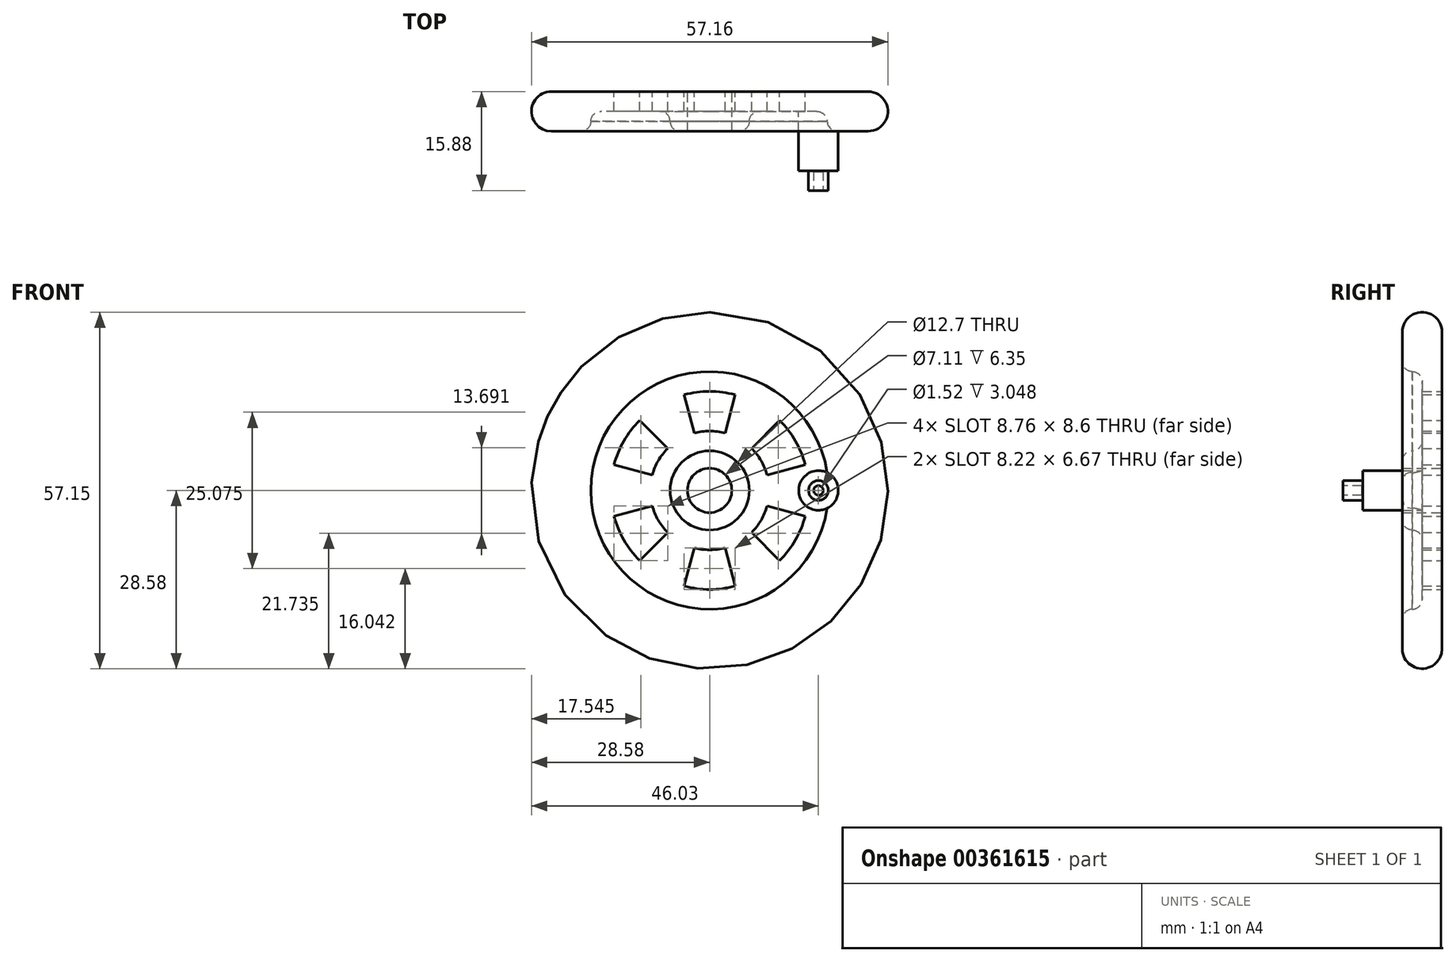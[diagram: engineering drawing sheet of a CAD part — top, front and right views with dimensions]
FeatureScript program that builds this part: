
annotation { "Feature Type Name" : "Feature", "Feature Type Description" : "" }
export const myFeature = defineFeature(function(context is Context, id is Id, definition is map)
    precondition{}
    {
        {
            var Q0;
            Q0=qCreatedBy(makeId("Top.planeOp"),FACE);
            var sketch = newSketch(context, id + "F0", { "sketchPlane" : qUnion([Q0])});
            skLineSegment(sketch, "E0", {"start": v(-3.56, 7.04) * mm, "end": v(-3.56, 0.69) * mm});
            skLineSegment(sketch, "E1", {"start": v(-3.56, 0.69) * mm, "end": v(-4.75, 0.69) * mm});
            skLineSegment(sketch, "E2", {"start": v(-6.35, 2.26) * mm, "end": v(-6.35, 2.29) * mm});
            skLineSegment(sketch, "E3", {"start": v(-7.95, 3.86) * mm, "end": v(-17.45, 3.86) * mm});
            skLineSegment(sketch, "E4", {"start": v(-19.05, 2.29) * mm, "end": v(-19.05, 2.26) * mm});
            skLineSegment(sketch, "E5", {"start": v(-20.65, 0.69) * mm, "end": v(-25.4, 0.69) * mm});
            skLineSegment(sketch, "E6", {"start": v(-25.4, 7.04) * mm, "end": v(-3.56, 7.04) * mm});
            skLineSegment(sketch, "E7", {"start": v(0, 5.87) * mm, "end": v(0, -4.8) * mm, "construction": true});
            skArc(sketch, "E8", {"start": v(-25.4, 7.04) * mm, "mid": v(-28.58, 3.86) * mm, "end": v(-25.4, 0.69) * mm});
            skPoint(sketch, "E9.visualSharp", {"position": v(-19.05, 0.69) * mm});
            skArc(sketch, "E9.filletArc", {"start": v(-20.65, 0.69) * mm, "mid": v(-19.52, 1.15) * mm, "end": v(-19.05, 2.29) * mm});
            skPoint(sketch, "E10.visualSharp", {"position": v(-19.05, 3.86) * mm});
            skArc(sketch, "E10.filletArc", {"start": v(-17.45, 3.86) * mm, "mid": v(-18.58, 3.4) * mm, "end": v(-19.05, 2.26) * mm});
            skPoint(sketch, "E11.visualSharp", {"position": v(-6.35, 3.86) * mm});
            skArc(sketch, "E11.filletArc", {"start": v(-6.35, 2.26) * mm, "mid": v(-6.82, 3.4) * mm, "end": v(-7.95, 3.86) * mm});
            skPoint(sketch, "E12.visualSharp", {"position": v(-6.35, 0.69) * mm});
            skArc(sketch, "E12.filletArc", {"start": v(-6.35, 2.29) * mm, "mid": v(-5.88, 1.15) * mm, "end": v(-4.75, 0.69) * mm});
            skSolve(sketch);
        }
        {
            var Q0;
            Q0 = qSketchRegion(id + "F0", true);
            var Q1;
            Q1=sQuery(id+"F0.wireOp",EDGE,"E7");
            revolve(context, id + "F1", {"entities" : qUnion([Q0]), "axis" : qUnion([Q1]), "revolveType" : RevolveType.FULL});
        }
        {
            var Q0;
            Q0=makeQuery(id+"F1.opRevolve","SWEPT_FACE",FACE,{"disambiguationData":[OSD([sQuery(id+"F0.wireOp",EDGE,"E6")])]});
            var sketch = newSketch(context, id + "F2", { "sketchPlane" : qUnion([Q0])});
            skArc(sketch, "E13", {"start": v(15.33, 4.1) * mm, "mid": v(13.75, 7.94) * mm, "end": v(11.23, 11.23) * mm});
            skArc(sketch, "E14", {"start": v(9.2, 2.47) * mm, "mid": v(8.25, 4.76) * mm, "end": v(6.74, 6.74) * mm});
            skLineSegment(sketch, "E15", {"start": v(6.74, 6.74) * mm, "end": v(11.23, 11.23) * mm});
            skLineSegment(sketch, "E16", {"start": v(9.2, 2.47) * mm, "end": v(15.33, 4.1) * mm});
            skArc(sketch, "E17.1.0", {"start": v(4.1, 15.33) * mm, "mid": v(0, 15.88) * mm, "end": v(-4.1, 15.33) * mm});
            skLineSegment(sketch, "E17.1.1", {"start": v(-2.47, 9.2) * mm, "end": v(-4.1, 15.33) * mm});
            skLineSegment(sketch, "E17.1.2", {"start": v(2.47, 9.2) * mm, "end": v(4.1, 15.33) * mm});
            skArc(sketch, "E17.1.3", {"start": v(2.47, 9.2) * mm, "mid": v(0, 9.53) * mm, "end": v(-2.47, 9.2) * mm});
            skArc(sketch, "E17.2.0", {"start": v(-11.23, 11.23) * mm, "mid": v(-13.75, 7.94) * mm, "end": v(-15.33, 4.1) * mm});
            skLineSegment(sketch, "E17.2.1", {"start": v(-9.2, 2.47) * mm, "end": v(-15.33, 4.1) * mm});
            skLineSegment(sketch, "E17.2.2", {"start": v(-6.74, 6.74) * mm, "end": v(-11.23, 11.23) * mm});
            skArc(sketch, "E17.2.3", {"start": v(-6.74, 6.74) * mm, "mid": v(-8.25, 4.76) * mm, "end": v(-9.2, 2.47) * mm});
            skArc(sketch, "E17.3.0", {"start": v(-15.33, -4.1) * mm, "mid": v(-13.75, -7.94) * mm, "end": v(-11.23, -11.23) * mm});
            skLineSegment(sketch, "E17.3.1", {"start": v(-6.74, -6.74) * mm, "end": v(-11.23, -11.23) * mm});
            skLineSegment(sketch, "E17.3.2", {"start": v(-9.2, -2.47) * mm, "end": v(-15.33, -4.1) * mm});
            skArc(sketch, "E17.3.3", {"start": v(-9.2, -2.47) * mm, "mid": v(-8.25, -4.76) * mm, "end": v(-6.74, -6.74) * mm});
            skArc(sketch, "E17.4.0", {"start": v(-4.1, -15.33) * mm, "mid": v(0, -15.88) * mm, "end": v(4.1, -15.33) * mm});
            skLineSegment(sketch, "E17.4.1", {"start": v(2.47, -9.2) * mm, "end": v(4.1, -15.33) * mm});
            skLineSegment(sketch, "E17.4.2", {"start": v(-2.47, -9.2) * mm, "end": v(-4.1, -15.33) * mm});
            skArc(sketch, "E17.4.3", {"start": v(-2.47, -9.2) * mm, "mid": v(0, -9.53) * mm, "end": v(2.47, -9.2) * mm});
            skArc(sketch, "E17.5.0", {"start": v(11.23, -11.23) * mm, "mid": v(13.75, -7.94) * mm, "end": v(15.33, -4.1) * mm});
            skLineSegment(sketch, "E17.5.1", {"start": v(9.2, -2.47) * mm, "end": v(15.33, -4.1) * mm});
            skLineSegment(sketch, "E17.5.2", {"start": v(6.74, -6.74) * mm, "end": v(11.23, -11.23) * mm});
            skArc(sketch, "E17.5.3", {"start": v(6.74, -6.74) * mm, "mid": v(8.25, -4.76) * mm, "end": v(9.2, -2.47) * mm});
            skSolve(sketch);
        }
        {
            var Q0;
            Q0 = qSketchRegion(id + "F2", true);
            extrude(context, id + "F3", {"entities" : qUnion([Q0]), "operationType" : NewBodyOperationType.REMOVE, "oppositeDirection" : true, "depth" : 25.4 * mm});
        }
        {
            var Q0;
            Q0=makeQuery(id+"F1.opRevolve","SWEPT_FACE",FACE,{"disambiguationData":[OSD([sQuery(id+"F0.wireOp",EDGE,"E3")])]});
            var sketch = newSketch(context, id + "F4", { "sketchPlane" : qUnion([Q0])});
            skCircle(sketch, "E18", {"center": v(17.45, 0) * mm, "radius": 3.18 * mm});
            skSolve(sketch);
        }
        {
            var Q0;
            Q0 = qSketchRegion(id + "F4", true);
            extrude(context, id + "F5", {"entities" : qUnion([Q0]), "operationType" : NewBodyOperationType.ADD, "depth" : 9.52 * mm});
        }
        {
            var Q0;
            Q0=makeQuery(id+"F5.opExtrude","CAP_FACE",FACE,{"disambiguationData":[OSD([sQuery(id+"F4.wireOp",EDGE,"E18")])],"isStart":false});
            var sketch = newSketch(context, id + "F6", { "sketchPlane" : qUnion([Q0])});
            skCircle(sketch, "E19", {"center": v(17.45, 0) * mm, "radius": 1.59 * mm});
            skSolve(sketch);
        }
        {
            var Q0;
            Q0=makeQuery(id+"F6.imprint","IMPRINT",FACE,{"disambiguationData":[TD([[makeQuery(id+"F6.imprint","IMPRINT",EDGE,{"derivedFrom":sQuery(id+"F6.wireOp",EDGE,"E19")}),1.0]])]});
            extrude(context, id + "F7", {"entities" : qUnion([Q0]), "operationType" : NewBodyOperationType.ADD, "depth" : 3.17 * mm});
        }
        {
            var Q0;
            Q0=makeQuery(id+"F7.opExtrude","CAP_FACE",FACE,{"disambiguationData":[OSD([sQuery(id+"F6.wireOp",EDGE,"E19")])],"isStart":false});
            var sketch = newSketch(context, id + "F8", { "sketchPlane" : qUnion([Q0])});
            skCircle(sketch, "E20", {"center": v(17.45, 0) * mm, "radius": 0.76 * mm});
            skSolve(sketch);
        }
        {
            var Q0;
            Q0 = qSketchRegion(id + "F8", true);
            extrude(context, id + "F9", {"entities" : qUnion([Q0]), "operationType" : NewBodyOperationType.REMOVE, "oppositeDirection" : true, "depth" : 3.05 * mm});
        }
    });
